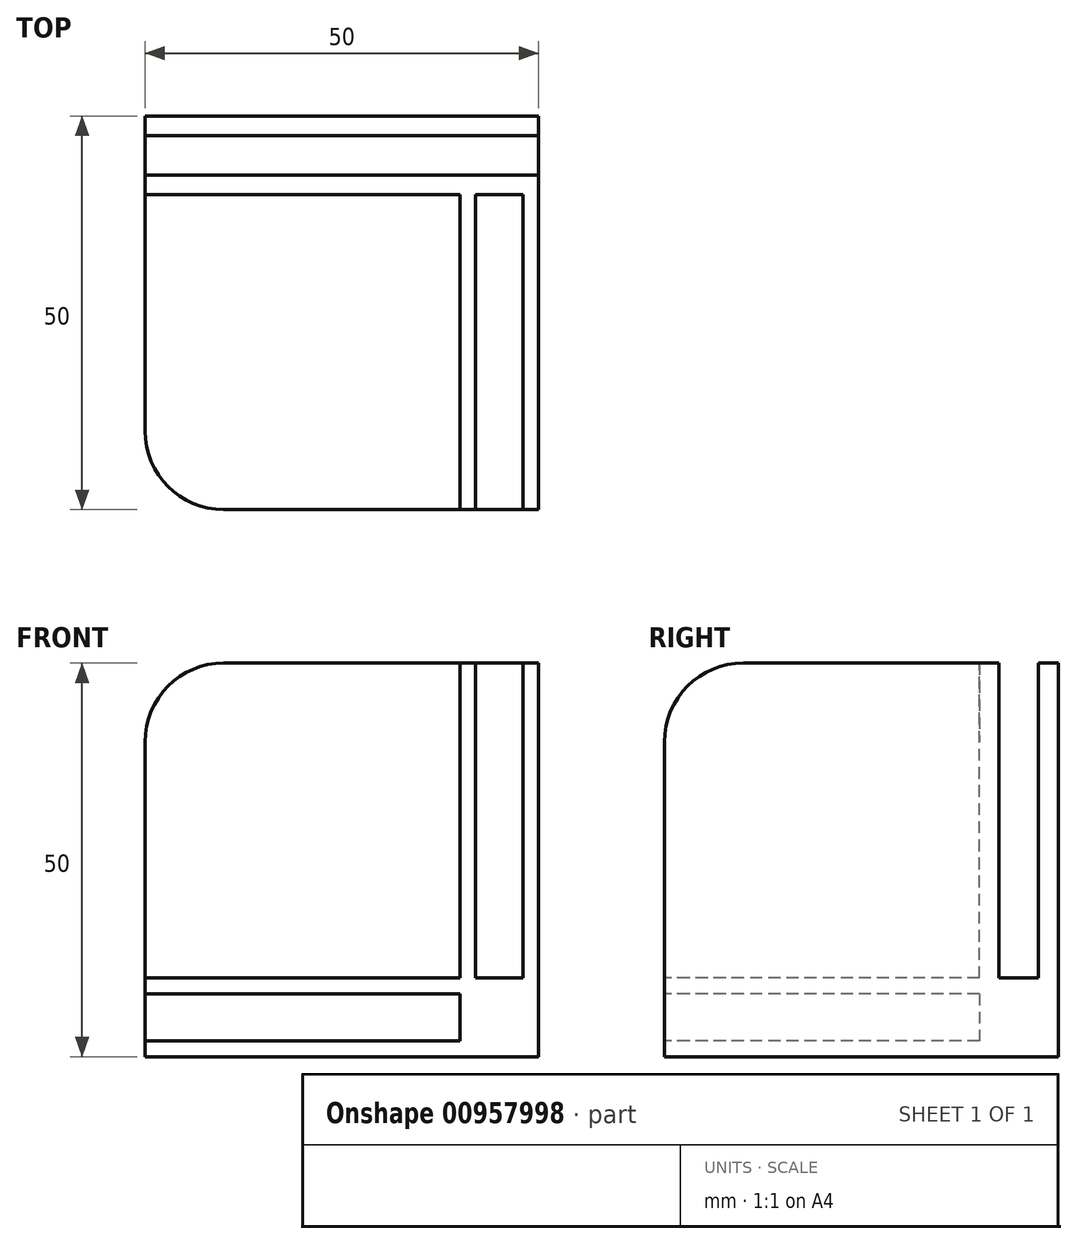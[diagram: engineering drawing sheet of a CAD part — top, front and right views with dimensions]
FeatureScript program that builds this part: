
annotation { "Feature Type Name" : "Feature", "Feature Type Description" : "" }
export const myFeature = defineFeature(function(context is Context, id is Id, definition is map)
    precondition{}
    {
        {
            var Q0;
            Q0=qCreatedBy(makeId("Top.planeOp"),FACE);
            var sketch = newSketch(context, id + "F0", { "sketchPlane" : qUnion([Q0])});
            skLineSegment(sketch, "E0.bottom", {"start": v(0, 0) * mm, "end": v(-50, 0) * mm});
            skLineSegment(sketch, "E0.top", {"start": v(0, -50) * mm, "end": v(-40, -50) * mm});
            skLineSegment(sketch, "E0.left", {"start": v(0, 0) * mm, "end": v(0, -50) * mm});
            skLineSegment(sketch, "E0.right", {"start": v(-50, 0) * mm, "end": v(-50, -40) * mm});
            skPoint(sketch, "E1.visualSharp", {"position": v(-50, -50) * mm});
            skArc(sketch, "E1.filletArc", {"start": v(-50, -40) * mm, "mid": v(-47.07, -47.07) * mm, "end": v(-40, -50) * mm});
            skSolve(sketch);
        }
        {
            var Q0;
            Q0=makeQuery(id+"F0.imprint","IMPRINT",FACE,{"disambiguationData":[TD([[makeQuery(id+"F0.imprint","IMPRINT",EDGE,{"derivedFrom":sQuery(id+"F0.wireOp",EDGE,"tNkWgY0K-5FoM-fzsk-HCrw-KOSka2LcS9h1.bottom")}),-1.0]])]});
            var Q1;
            Q1=makeQuery(id+"F0.imprint","IMPRINT",FACE,{"disambiguationData":[TD([[makeQuery(id+"F0.imprint","IMPRINT",EDGE,{"derivedFrom":sQuery(id+"F0.wireOp",EDGE,"E0.bottom")}),1.0]])]});
            var Q2;
            Q2=makeQuery(id+"F0.imprint","IMPRINT",FACE,{"disambiguationData":[TD([[makeQuery(id+"F0.imprint","IMPRINT",EDGE,{"derivedFrom":sQuery(id+"F0.wireOp",EDGE,"E0.top")}),-1.0]])]});
            var Q3;
            Q3=makeQuery(id+"F0.imprint","IMPRINT",FACE,{"disambiguationData":[TD([[makeQuery(id+"F0.imprint","IMPRINT",EDGE,{"derivedFrom":sQuery(id+"F0.wireOp",EDGE,"fvIwUqZD-S5C8-yHxi-N0ak-uGxWySerV2bo.bottom")}),1.0]])]});
            var Q4;
            Q4=makeQuery(id+"F0.imprint","IMPRINT",FACE,{"disambiguationData":[TD([[makeQuery(id+"F0.imprint","IMPRINT",EDGE,{"derivedFrom":sQuery(id+"F0.wireOp",EDGE,"JSCxDXyh-nDxv-V0qH-dKlW-7TGNpykFalIj.bottom")}),1.0]])]});
            extrude(context, id + "F1", {"entities" : qUnion([Q0, Q1, Q2, Q3, Q4]), "depth" : 10 * mm, "offsetDistance" : 25 * mm});
        }
        {
            var Q0;
            Q0=qCreatedBy(makeId("Right.planeOp"),FACE);
            var sketch = newSketch(context, id + "F2", { "sketchPlane" : qUnion([Q0])});
            skLineSegment(sketch, "E2.bottom", {"start": v(0, 10) * mm, "end": v(-50, 10) * mm});
            skLineSegment(sketch, "E2.top", {"start": v(0, 50) * mm, "end": v(-40, 50) * mm});
            skLineSegment(sketch, "E2.left", {"start": v(0, 10) * mm, "end": v(0, 50) * mm});
            skLineSegment(sketch, "E2.right", {"start": v(-50, 10) * mm, "end": v(-50, 40) * mm});
            skPoint(sketch, "E3.visualSharp", {"position": v(-50, 50) * mm});
            skArc(sketch, "E3.filletArc", {"start": v(-40, 50) * mm, "mid": v(-47.07, 47.07) * mm, "end": v(-50, 40) * mm});
            skSolve(sketch);
        }
        {
            var Q0;
            Q0=makeQuery(id+"F2.imprint","IMPRINT",FACE,{"disambiguationData":[TD([[makeQuery(id+"F2.imprint","IMPRINT",EDGE,{"derivedFrom":sQuery(id+"F2.wireOp",EDGE,"E2.bottom")}),-1.0]])]});
            extrude(context, id + "F3", {"entities" : qUnion([Q0]), "operationType" : NewBodyOperationType.ADD, "oppositeDirection" : true, "depth" : 10 * mm, "offsetDistance" : 25 * mm});
        }
        {
            var Q0;
            Q0=qCreatedBy(makeId("Front.planeOp"),FACE);
            var sketch = newSketch(context, id + "F4", { "sketchPlane" : qUnion([Q0])});
            skLineSegment(sketch, "E4.bottom", {"start": v(-10, 10) * mm, "end": v(-50, 10) * mm});
            skLineSegment(sketch, "E4.top", {"start": v(-10, 50) * mm, "end": v(-40, 50) * mm});
            skLineSegment(sketch, "E4.left", {"start": v(-10, 10) * mm, "end": v(-10, 50) * mm});
            skLineSegment(sketch, "E4.right", {"start": v(-50, 10) * mm, "end": v(-50, 40) * mm});
            skPoint(sketch, "E5.visualSharp", {"position": v(-50, 50) * mm});
            skArc(sketch, "E5.filletArc", {"start": v(-40, 50) * mm, "mid": v(-47.07, 47.07) * mm, "end": v(-50, 40) * mm});
            skSolve(sketch);
        }
        {
            var Q0;
            Q0=makeQuery(id+"F4.imprint","IMPRINT",FACE,{"disambiguationData":[TD([[makeQuery(id+"F4.imprint","IMPRINT",EDGE,{"derivedFrom":sQuery(id+"F4.wireOp",EDGE,"E4.bottom")}),-1.0]])]});
            extrude(context, id + "F5", {"entities" : qUnion([Q0]), "operationType" : NewBodyOperationType.ADD, "depth" : 10 * mm, "offsetDistance" : 25 * mm});
        }
        {
            var Q0;
            Q0=makeQuery(id+"F3.boolean.opBoolean","MERGE",FACE,{"derivedFrom":[makeQuery(id+"F1.opExtrude","SWEPT_FACE",FACE,{"disambiguationData":[OSD([sQuery(id+"F0.wireOp",EDGE,"E0.top")])]}),makeQuery(id+"F3.opExtrude","SWEPT_FACE",FACE,{"disambiguationData":[OSD([sQuery(id+"F2.wireOp",EDGE,"E2.right")])]})]});
            var sketch = newSketch(context, id + "F6", { "sketchPlane" : qUnion([Q0])});
            skLineSegment(sketch, "E6.bottom", {"start": v(-10, 2) * mm, "end": v(-60, 2) * mm});
            skLineSegment(sketch, "E6.top", {"start": v(-10, 8) * mm, "end": v(-60, 8) * mm});
            skLineSegment(sketch, "E6.left", {"start": v(-10, 2) * mm, "end": v(-10, 8) * mm});
            skLineSegment(sketch, "E6.right", {"start": v(-60, 2) * mm, "end": v(-60, 8) * mm});
            skLineSegment(sketch, "E7.bottom", {"start": v(-10, 2) * mm, "end": v(-15, 2) * mm});
            skLineSegment(sketch, "E7.top", {"start": v(-10, 52) * mm, "end": v(-15, 52) * mm});
            skLineSegment(sketch, "E8.bottom", {"start": v(-2, 10) * mm, "end": v(-8, 10) * mm});
            skLineSegment(sketch, "E8.top", {"start": v(-2, 60) * mm, "end": v(-8, 60) * mm});
            skLineSegment(sketch, "E8.left", {"start": v(-2, 10) * mm, "end": v(-2, 60) * mm});
            skLineSegment(sketch, "E8.right", {"start": v(-8, 10) * mm, "end": v(-8, 60) * mm});
            skSolve(sketch);
        }
        {
            var Q0;
            {var subQ0=sQuery(id+"F6.wireOp",EDGE,"E6.left");Q0=makeQuery(id+"F6.imprint","IMPRINT",FACE,{"disambiguationData":[TD([[makeQuery(id+"F6.imprint","IMPRINT",EDGE,{"derivedFrom":subQ0}),1.0]])]});}
            var Q1;
            {var subQ0=sQuery(id+"F6.wireOp",EDGE,"E6.right");Q1=makeQuery(id+"F6.imprint","IMPRINT",FACE,{"disambiguationData":[TD([[makeQuery(id+"F6.imprint","IMPRINT",EDGE,{"derivedFrom":subQ0}),-1.0]])]});}
            var Q2;
            {var subQ0=sQuery(id+"F6.wireOp",EDGE,"E6.right");Q2=makeQuery(id+"F6.imprint","IMPRINT",FACE,{"disambiguationData":[TD([[makeQuery(id+"F6.imprint","IMPRINT",EDGE,{"derivedFrom":subQ0}),-1.0]])]});}
            var Q3;
            {var subQ0=sQuery(id+"F6.wireOp",EDGE,"E8.bottom");Q3=makeQuery(id+"F6.imprint","IMPRINT",FACE,{"disambiguationData":[TD([[makeQuery(id+"F6.imprint","IMPRINT",EDGE,{"derivedFrom":subQ0}),-1.0]])]});}
            var Q4;
            {var subQ0=sQuery(id+"F6.wireOp",EDGE,"E8.top");Q4=makeQuery(id+"F6.imprint","IMPRINT",FACE,{"disambiguationData":[TD([[makeQuery(id+"F6.imprint","IMPRINT",EDGE,{"derivedFrom":subQ0}),1.0]])]});}
            extrude(context, id + "F7", {"entities" : qUnion([Q0, Q1, Q2, Q3, Q4]), "operationType" : NewBodyOperationType.REMOVE, "oppositeDirection" : true, "depth" : 40 * mm, "offsetDistance" : 25 * mm});
        }
        {
            var Q0;
            Q0=makeQuery(id+"F5.boolean.opBoolean","MERGE",FACE,{"derivedFrom":[makeQuery(id+"F3.opExtrude","SWEPT_FACE",FACE,{"disambiguationData":[OSD([sQuery(id+"F2.wireOp",EDGE,"E2.top")])]}),makeQuery(id+"F5.opExtrude","SWEPT_FACE",FACE,{"disambiguationData":[OSD([sQuery(id+"F4.wireOp",EDGE,"E4.top")])]})]});
            var sketch = newSketch(context, id + "F8", { "sketchPlane" : qUnion([Q0])});
            skLineSegment(sketch, "E9.bottom", {"start": v(5, -2.5) * mm, "end": v(-55, -2.5) * mm});
            skLineSegment(sketch, "E9.top", {"start": v(5, -7.5) * mm, "end": v(-55, -7.5) * mm});
            skLineSegment(sketch, "E9.left", {"start": v(5, -2.5) * mm, "end": v(5, -7.5) * mm});
            skLineSegment(sketch, "E9.right", {"start": v(-55, -2.5) * mm, "end": v(-55, -7.5) * mm});
            skSolve(sketch);
        }
        {
            var Q0;
            {var subQ0=sQuery(id+"F8.wireOp",EDGE,"E9.left");Q0=makeQuery(id+"F8.imprint","IMPRINT",FACE,{"disambiguationData":[TD([[makeQuery(id+"F8.imprint","IMPRINT",EDGE,{"derivedFrom":subQ0}),-1.0]])]});}
            var Q1;
            {var subQ0=sQuery(id+"F8.wireOp",EDGE,"E9.right");Q1=makeQuery(id+"F8.imprint","IMPRINT",FACE,{"disambiguationData":[TD([[makeQuery(id+"F8.imprint","IMPRINT",EDGE,{"derivedFrom":subQ0}),1.0]])]});}
            var Q2;
            {var subQ0=sQuery(id+"F8.wireOp",EDGE,"E9.bottom");var subQ1=makeQuery(id+"F3.opExtrude","CAP_EDGE",EDGE,{"disambiguationData":[OSD([sQuery(id+"F2.wireOp",EDGE,"E2.top")])],"isStart":true});var subQ2=makeQuery(id+"F8.imprint","INTERSECT",VERTEX,{"derivedFrom":[subQ1,subQ0]});Q2=makeQuery(id+"F8.imprint","IMPRINT",FACE,{"disambiguationData":[TD([[makeQuery(id+"F8.imprint","IMPRINT",EDGE,{"disambiguationData":[TD([[subQ2,-1.0]])],"derivedFrom":subQ1}),-1.0]])]});}
            extrude(context, id + "F9", {"entities" : qUnion([Q0, Q1, Q2]), "operationType" : NewBodyOperationType.REMOVE, "oppositeDirection" : true, "depth" : 40 * mm, "offsetDistance" : 25 * mm});
        }
    });
